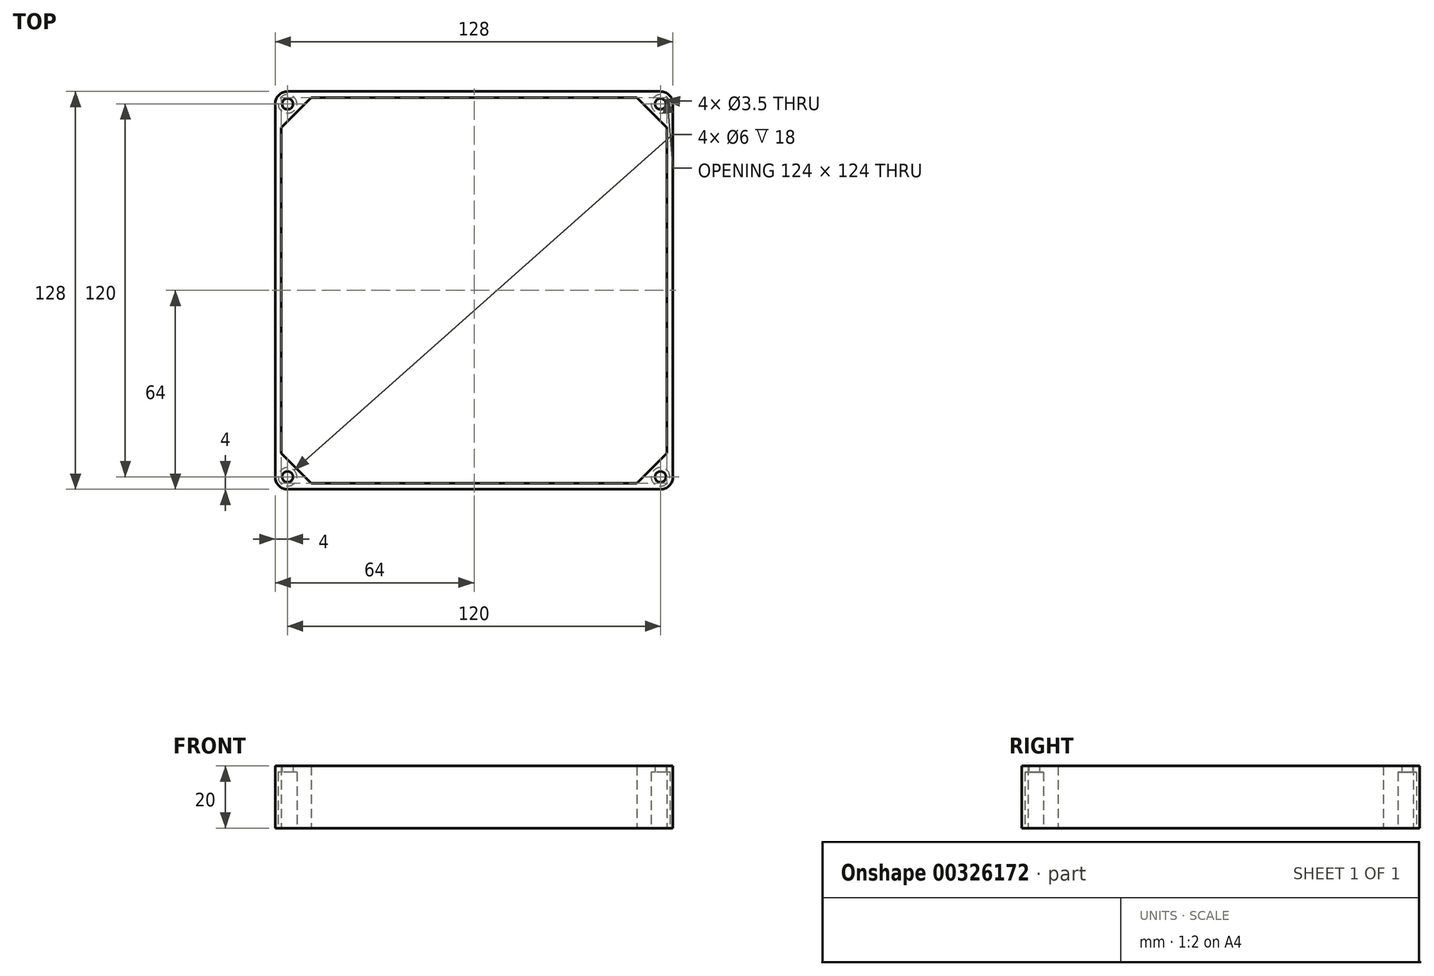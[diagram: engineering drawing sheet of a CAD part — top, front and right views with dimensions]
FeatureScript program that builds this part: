
annotation { "Feature Type Name" : "Feature", "Feature Type Description" : "" }
export const myFeature = defineFeature(function(context is Context, id is Id, definition is map)
    precondition{}
    {
        {
            var Q0;
            Q0=qCreatedBy(makeId("Top.planeOp"),FACE);
            var sketch = newSketch(context, id + "F0", { "sketchPlane" : qUnion([Q0])});
            skCircle(sketch, "E0", {"center": v(-60, 60) * mm, "radius": 1.75 * mm});
            skCircle(sketch, "E1", {"center": v(-60, 60) * mm, "radius": 3 * mm});
            skCircle(sketch, "E2", {"center": v(-60, 60) * mm, "radius": 4 * mm});
            skCircle(sketch, "E3.0.1.0", {"center": v(-60, -60) * mm, "radius": 4 * mm});
            skCircle(sketch, "E3.0.1.1", {"center": v(-60, -60) * mm, "radius": 3 * mm});
            skCircle(sketch, "E3.0.1.2", {"center": v(-60, -60) * mm, "radius": 1.75 * mm});
            skCircle(sketch, "E3.1.0.0", {"center": v(60, 60) * mm, "radius": 4 * mm});
            skCircle(sketch, "E3.1.0.1", {"center": v(60, 60) * mm, "radius": 3 * mm});
            skCircle(sketch, "E3.1.0.2", {"center": v(60, 60) * mm, "radius": 1.75 * mm});
            skCircle(sketch, "E3.1.1.0", {"center": v(60, -60) * mm, "radius": 4 * mm});
            skCircle(sketch, "E3.1.1.1", {"center": v(60, -60) * mm, "radius": 3 * mm});
            skCircle(sketch, "E3.1.1.2", {"center": v(60, -60) * mm, "radius": 1.75 * mm});
            skLineSegment(sketch, "E3.direction1", {"start": v(-60, 60) * mm, "end": v(-56, 60) * mm, "construction": true});
            skLineSegment(sketch, "E3.direction2", {"start": v(-60, 60) * mm, "end": v(-60, 56) * mm, "construction": true});
            skLineSegment(sketch, "E4", {"start": v(-64, 60) * mm, "end": v(-64, -60) * mm});
            skLineSegment(sketch, "E5", {"start": v(-60, -64) * mm, "end": v(60, -64) * mm});
            skLineSegment(sketch, "E6", {"start": v(64, -60) * mm, "end": v(64, 60) * mm});
            skLineSegment(sketch, "E7", {"start": v(60, 64) * mm, "end": v(-60, 64) * mm});
            skLineSegment(sketch, "E8", {"start": v(62, -56.54) * mm, "end": v(62, 56.54) * mm});
            skLineSegment(sketch, "E9", {"start": v(56.54, 62) * mm, "end": v(-56.54, 62) * mm});
            skLineSegment(sketch, "E10", {"start": v(-62, 56.54) * mm, "end": v(-62, -56.54) * mm});
            skLineSegment(sketch, "E11", {"start": v(56.54, -62) * mm, "end": v(-56.54, -62) * mm});
            skPoint(sketch, "E12.start.orphan", {"position": v(60, -56) * mm});
            skLineSegment(sketch, "E13.trimOffspring", {"start": v(56, 60) * mm, "end": v(60, 60) * mm, "construction": true});
            skLineSegment(sketch, "E14.trimOffspring", {"start": v(-60, -56) * mm, "end": v(-60, -60) * mm, "construction": true});
            skPoint(sketch, "E15.end.orphan", {"position": v(56, -60) * mm});
            skPoint(sketch, "E15.start.orphan", {"position": v(-56, -60) * mm});
            skLineSegment(sketch, "E16", {"start": v(-52.34, -62) * mm, "end": v(-62, -52.34) * mm});
            skLineSegment(sketch, "E17", {"start": v(62, -52.34) * mm, "end": v(52.34, -62) * mm});
            skLineSegment(sketch, "E18", {"start": v(62, 52.34) * mm, "end": v(52.34, 62) * mm});
            skLineSegment(sketch, "E19", {"start": v(-52.34, 62) * mm, "end": v(-62, 52.34) * mm});
            skSolve(sketch);
        }
        {
            var Q0;
            {var subQ0=sQuery(id+"F0.wireOp",EDGE,"E4");Q0=makeQuery(id+"F0.imprint","IMPRINT",FACE,{"disambiguationData":[TD([[makeQuery(id+"F0.imprint","IMPRINT",EDGE,{"derivedFrom":subQ0}),1.0]])]});}
            var Q1;
            {var subQ0=sQuery(id+"F0.wireOp",EDGE,"E5");Q1=makeQuery(id+"F0.imprint","IMPRINT",FACE,{"disambiguationData":[TD([[makeQuery(id+"F0.imprint","IMPRINT",EDGE,{"derivedFrom":subQ0}),1.0]])]});}
            var Q2;
            {var subQ0=sQuery(id+"F0.wireOp",EDGE,"E6");Q2=makeQuery(id+"F0.imprint","IMPRINT",FACE,{"disambiguationData":[TD([[makeQuery(id+"F0.imprint","IMPRINT",EDGE,{"derivedFrom":subQ0}),1.0]])]});}
            var Q3;
            Q3=makeQuery(id+"F0.imprint","IMPRINT",FACE,{"disambiguationData":[TD([[makeQuery(id+"F0.imprint","IMPRINT",EDGE,{"derivedFrom":sQuery(id+"F0.wireOp",EDGE,"E3.0.1.1")}),-1.0]])]});
            var Q4;
            Q4=makeQuery(id+"F0.imprint","IMPRINT",FACE,{"disambiguationData":[TD([[makeQuery(id+"F0.imprint","IMPRINT",EDGE,{"derivedFrom":sQuery(id+"F0.wireOp",EDGE,"E3.0.1.1")}),1.0]])]});
            var Q5;
            Q5=makeQuery(id+"F0.imprint","IMPRINT",FACE,{"disambiguationData":[TD([[makeQuery(id+"F0.imprint","IMPRINT",EDGE,{"derivedFrom":sQuery(id+"F0.wireOp",EDGE,"E3.1.1.1")}),-1.0]])]});
            var Q6;
            Q6=makeQuery(id+"F0.imprint","IMPRINT",FACE,{"disambiguationData":[TD([[makeQuery(id+"F0.imprint","IMPRINT",EDGE,{"derivedFrom":sQuery(id+"F0.wireOp",EDGE,"E3.1.1.1")}),1.0]])]});
            var Q7;
            {var subQ0=sQuery(id+"F0.wireOp",EDGE,"E7");Q7=makeQuery(id+"F0.imprint","IMPRINT",FACE,{"disambiguationData":[TD([[makeQuery(id+"F0.imprint","IMPRINT",EDGE,{"derivedFrom":subQ0}),1.0]])]});}
            var Q8;
            Q8=makeQuery(id+"F0.imprint","IMPRINT",FACE,{"disambiguationData":[TD([[makeQuery(id+"F0.imprint","IMPRINT",EDGE,{"derivedFrom":sQuery(id+"F0.wireOp",EDGE,"E1")}),-1.0]])]});
            var Q9;
            Q9=makeQuery(id+"F0.imprint","IMPRINT",FACE,{"disambiguationData":[TD([[makeQuery(id+"F0.imprint","IMPRINT",EDGE,{"derivedFrom":sQuery(id+"F0.wireOp",EDGE,"E0")}),-1.0]])]});
            var Q10;
            Q10=makeQuery(id+"F0.imprint","IMPRINT",FACE,{"disambiguationData":[TD([[makeQuery(id+"F0.imprint","IMPRINT",EDGE,{"derivedFrom":sQuery(id+"F0.wireOp",EDGE,"E3.1.0.1")}),-1.0]])]});
            var Q11;
            Q11=makeQuery(id+"F0.imprint","IMPRINT",FACE,{"disambiguationData":[TD([[makeQuery(id+"F0.imprint","IMPRINT",EDGE,{"derivedFrom":sQuery(id+"F0.wireOp",EDGE,"E3.1.0.1")}),1.0]])]});
            var Q12;
            {var subQ0=sQuery(id+"F0.wireOp",EDGE,"E9");var subQ1=sQuery(id+"F0.wireOp",EDGE,"E3.1.0.0");var subQ2=makeQuery(id+"F0.imprint","INTERSECT",VERTEX,{"derivedFrom":[subQ1,subQ0]});Q12=makeQuery(id+"F0.imprint","IMPRINT",FACE,{"disambiguationData":[TD([[makeQuery(id+"F0.imprint","IMPRINT",EDGE,{"disambiguationData":[TD([[subQ2,-1.0]])],"derivedFrom":subQ1}),-1.0]])]});}
            var Q13;
            {var subQ0=sQuery(id+"F0.wireOp",EDGE,"E8");var subQ1=sQuery(id+"F0.wireOp",EDGE,"E3.1.0.0");var subQ2=makeQuery(id+"F0.imprint","INTERSECT",VERTEX,{"derivedFrom":[subQ1,subQ0]});Q13=makeQuery(id+"F0.imprint","IMPRINT",FACE,{"disambiguationData":[TD([[makeQuery(id+"F0.imprint","IMPRINT",EDGE,{"disambiguationData":[TD([[subQ2,1.0]])],"derivedFrom":subQ1}),-1.0]])]});}
            var Q14;
            {var subQ0=sQuery(id+"F0.wireOp",EDGE,"E9");var subQ1=sQuery(id+"F0.wireOp",EDGE,"E2");var subQ2=makeQuery(id+"F0.imprint","INTERSECT",VERTEX,{"derivedFrom":[subQ1,subQ0]});Q14=makeQuery(id+"F0.imprint","IMPRINT",FACE,{"disambiguationData":[TD([[makeQuery(id+"F0.imprint","IMPRINT",EDGE,{"disambiguationData":[TD([[subQ2,1.0]])],"derivedFrom":subQ1}),-1.0]])]});}
            var Q15;
            {var subQ0=sQuery(id+"F0.wireOp",EDGE,"E10");var subQ1=sQuery(id+"F0.wireOp",EDGE,"E2");var subQ2=makeQuery(id+"F0.imprint","INTERSECT",VERTEX,{"derivedFrom":[subQ1,subQ0]});Q15=makeQuery(id+"F0.imprint","IMPRINT",FACE,{"disambiguationData":[TD([[makeQuery(id+"F0.imprint","IMPRINT",EDGE,{"disambiguationData":[TD([[subQ2,-1.0]])],"derivedFrom":subQ1}),-1.0]])]});}
            var Q16;
            {var subQ0=sQuery(id+"F0.wireOp",EDGE,"E8");var subQ1=sQuery(id+"F0.wireOp",EDGE,"E3.1.1.0");var subQ2=makeQuery(id+"F0.imprint","INTERSECT",VERTEX,{"derivedFrom":[subQ1,subQ0]});Q16=makeQuery(id+"F0.imprint","IMPRINT",FACE,{"disambiguationData":[TD([[makeQuery(id+"F0.imprint","IMPRINT",EDGE,{"disambiguationData":[TD([[subQ2,-1.0]])],"derivedFrom":subQ1}),-1.0]])]});}
            var Q17;
            {var subQ0=sQuery(id+"F0.wireOp",EDGE,"E11");var subQ1=sQuery(id+"F0.wireOp",EDGE,"E3.1.1.0");var subQ2=makeQuery(id+"F0.imprint","INTERSECT",VERTEX,{"derivedFrom":[subQ1,subQ0]});Q17=makeQuery(id+"F0.imprint","IMPRINT",FACE,{"disambiguationData":[TD([[makeQuery(id+"F0.imprint","IMPRINT",EDGE,{"disambiguationData":[TD([[subQ2,1.0]])],"derivedFrom":subQ1}),-1.0]])]});}
            var Q18;
            {var subQ0=sQuery(id+"F0.wireOp",EDGE,"E11");var subQ1=sQuery(id+"F0.wireOp",EDGE,"E3.0.1.0");var subQ2=makeQuery(id+"F0.imprint","INTERSECT",VERTEX,{"derivedFrom":[subQ1,subQ0]});Q18=makeQuery(id+"F0.imprint","IMPRINT",FACE,{"disambiguationData":[TD([[makeQuery(id+"F0.imprint","IMPRINT",EDGE,{"disambiguationData":[TD([[subQ2,-1.0]])],"derivedFrom":subQ1}),-1.0]])]});}
            var Q19;
            {var subQ0=sQuery(id+"F0.wireOp",EDGE,"E10");var subQ1=sQuery(id+"F0.wireOp",EDGE,"E3.0.1.0");var subQ2=makeQuery(id+"F0.imprint","INTERSECT",VERTEX,{"derivedFrom":[subQ1,subQ0]});Q19=makeQuery(id+"F0.imprint","IMPRINT",FACE,{"disambiguationData":[TD([[makeQuery(id+"F0.imprint","IMPRINT",EDGE,{"disambiguationData":[TD([[subQ2,1.0]])],"derivedFrom":subQ1}),-1.0]])]});}
            extrude(context, id + "F1", {"entities" : qUnion([Q0, Q1, Q2, Q3, Q4, Q5, Q6, Q7, Q8, Q9, Q10, Q11, Q12, Q13, Q14, Q15, Q16, Q17, Q18, Q19]), "depth" : 20 * mm});
        }
        {
            var Q0;
            Q0=makeQuery(id+"F0.imprint","IMPRINT",FACE,{"disambiguationData":[TD([[makeQuery(id+"F0.imprint","IMPRINT",EDGE,{"derivedFrom":sQuery(id+"F0.wireOp",EDGE,"E3.1.1.1")}),1.0]])]});
            var Q1;
            Q1=makeQuery(id+"F0.imprint","IMPRINT",FACE,{"disambiguationData":[TD([[makeQuery(id+"F0.imprint","IMPRINT",EDGE,{"derivedFrom":sQuery(id+"F0.wireOp",EDGE,"E3.0.1.1")}),1.0]])]});
            var Q2;
            Q2=makeQuery(id+"F0.imprint","IMPRINT",FACE,{"disambiguationData":[TD([[makeQuery(id+"F0.imprint","IMPRINT",EDGE,{"derivedFrom":sQuery(id+"F0.wireOp",EDGE,"E0")}),-1.0]])]});
            var Q3;
            Q3=makeQuery(id+"F0.imprint","IMPRINT",FACE,{"disambiguationData":[TD([[makeQuery(id+"F0.imprint","IMPRINT",EDGE,{"derivedFrom":sQuery(id+"F0.wireOp",EDGE,"E3.1.0.1")}),1.0]])]});
            extrude(context, id + "F2", {"entities" : qUnion([Q0, Q1, Q2, Q3]), "operationType" : NewBodyOperationType.REMOVE, "depth" : 18 * mm});
        }
    });
